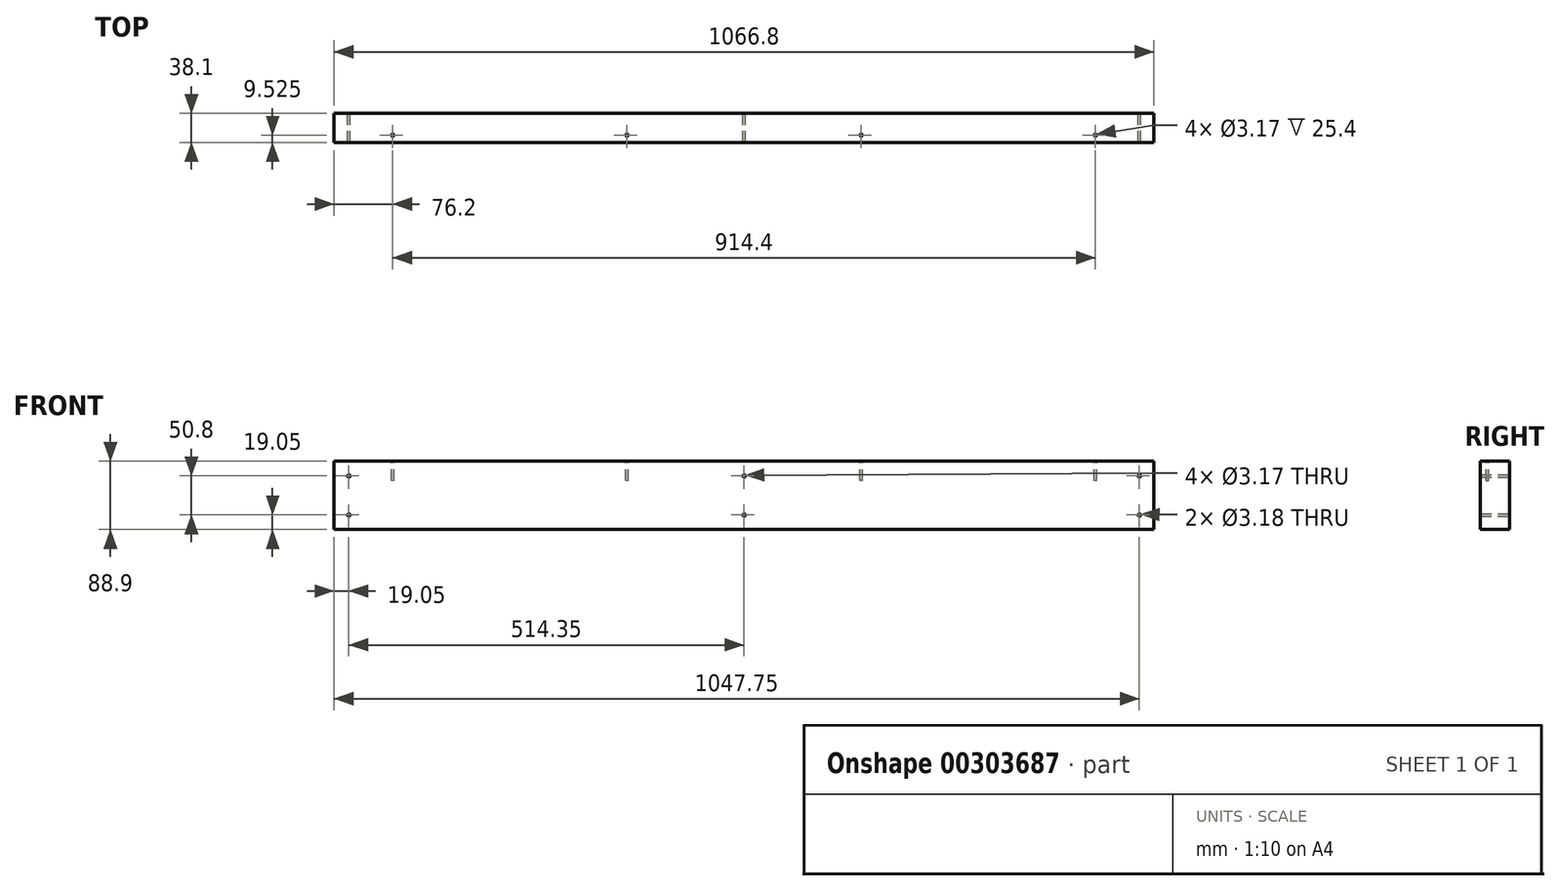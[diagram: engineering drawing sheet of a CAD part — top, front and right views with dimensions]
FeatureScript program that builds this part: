
annotation { "Feature Type Name" : "Feature", "Feature Type Description" : "" }
export const myFeature = defineFeature(function(context is Context, id is Id, definition is map)
    precondition{}
    {
        {
            var Q0;
            Q0=qCreatedBy(makeId("Front.planeOp"),FACE);
            var sketch = newSketch(context, id + "F0", { "sketchPlane" : qUnion([Q0])});
            skLineSegment(sketch, "E0.bottom", {"start": v(0, 0) * mm, "end": v(1066.8, 0) * mm});
            skLineSegment(sketch, "E0.top", {"start": v(0, -88.9) * mm, "end": v(1066.8, -88.9) * mm});
            skLineSegment(sketch, "E0.left", {"start": v(0, 0) * mm, "end": v(0, -88.9) * mm});
            skLineSegment(sketch, "E0.right", {"start": v(1066.8, 0) * mm, "end": v(1066.8, -88.9) * mm});
            skSolve(sketch);
        }
        {
            var Q0;
            Q0=qSketchRegion(id+"F0",true);
            extrude(context, id + "F1", {"entities" : qUnion([Q0]), "depth" : 38.1 * mm});
        }
        {
            var Q0;
            Q0=qCreatedBy(makeId("Top.planeOp"),FACE);
            var sketch = newSketch(context, id + "F2", { "sketchPlane" : qUnion([Q0])});
            skCircle(sketch, "E1", {"center": v(76.2, -28.57) * mm, "radius": 1.59 * mm});
            skCircle(sketch, "E2.1.0.0", {"center": v(381, -28.57) * mm, "radius": 1.59 * mm});
            skCircle(sketch, "E2.2.0.0", {"center": v(685.8, -28.57) * mm, "radius": 1.59 * mm});
            skCircle(sketch, "E2.3.0.0", {"center": v(990.6, -28.57) * mm, "radius": 1.59 * mm});
            skLineSegment(sketch, "E2.direction1", {"start": v(76.2, -28.57) * mm, "end": v(381, -28.57) * mm, "construction": true});
            skSolve(sketch);
        }
        {
            var Q0;
            Q0=makeQuery(id+"F2.imprint","IMPRINT",FACE,{"disambiguationData":[TD([[makeQuery(id+"F2.imprint","IMPRINT",EDGE,{"derivedFrom":sQuery(id+"F2.wireOp",EDGE,"E1")}),1.0]])]});
            var Q1;
            Q1=makeQuery(id+"F2.imprint","IMPRINT",FACE,{"disambiguationData":[TD([[makeQuery(id+"F2.imprint","IMPRINT",EDGE,{"derivedFrom":sQuery(id+"F2.wireOp",EDGE,"E2.1.0.0")}),1.0]])]});
            var Q2;
            Q2=makeQuery(id+"F2.imprint","IMPRINT",FACE,{"disambiguationData":[TD([[makeQuery(id+"F2.imprint","IMPRINT",EDGE,{"derivedFrom":sQuery(id+"F2.wireOp",EDGE,"E2.2.0.0")}),1.0]])]});
            var Q3;
            Q3=makeQuery(id+"F2.imprint","IMPRINT",FACE,{"disambiguationData":[TD([[makeQuery(id+"F2.imprint","IMPRINT",EDGE,{"derivedFrom":sQuery(id+"F2.wireOp",EDGE,"E2.3.0.0")}),1.0]])]});
            extrude(context, id + "F3", {"entities" : qUnion([Q0, Q1, Q2, Q3]), "operationType" : NewBodyOperationType.REMOVE, "oppositeDirection" : true, "depth" : 25.4 * mm});
        }
        {
            var Q0;
            Q0=qCreatedBy(makeId("Front.planeOp"),FACE);
            var sketch = newSketch(context, id + "F4", { "sketchPlane" : qUnion([Q0])});
            skCircle(sketch, "E3", {"center": v(19.05, -19.05) * mm, "radius": 1.59 * mm});
            skCircle(sketch, "E4.0.1.0", {"center": v(19.05, -69.85) * mm, "radius": 1.59 * mm});
            skCircle(sketch, "E4.1.0.0", {"center": v(533.4, -19.05) * mm, "radius": 1.59 * mm});
            skCircle(sketch, "E4.1.1.0", {"center": v(533.4, -69.85) * mm, "radius": 1.59 * mm});
            skCircle(sketch, "E4.2.0.0", {"center": v(1047.75, -19.05) * mm, "radius": 1.59 * mm});
            skCircle(sketch, "E4.2.1.0", {"center": v(1047.75, -69.85) * mm, "radius": 1.59 * mm});
            skLineSegment(sketch, "E4.direction1", {"start": v(19.05, -19.05) * mm, "end": v(533.4, -19.05) * mm, "construction": true});
            skLineSegment(sketch, "E4.direction2", {"start": v(19.05, -19.05) * mm, "end": v(19.05, -69.85) * mm, "construction": true});
            skSolve(sketch);
        }
        {
            var Q0;
            Q0 = qSketchRegion(id + "F4", true);
            extrude(context, id + "F5", {"entities" : qUnion([Q0]), "operationType" : NewBodyOperationType.REMOVE, "endBound" : BoundingType.THROUGH_ALL, "depth" : 25.4 * mm});
        }
    });
